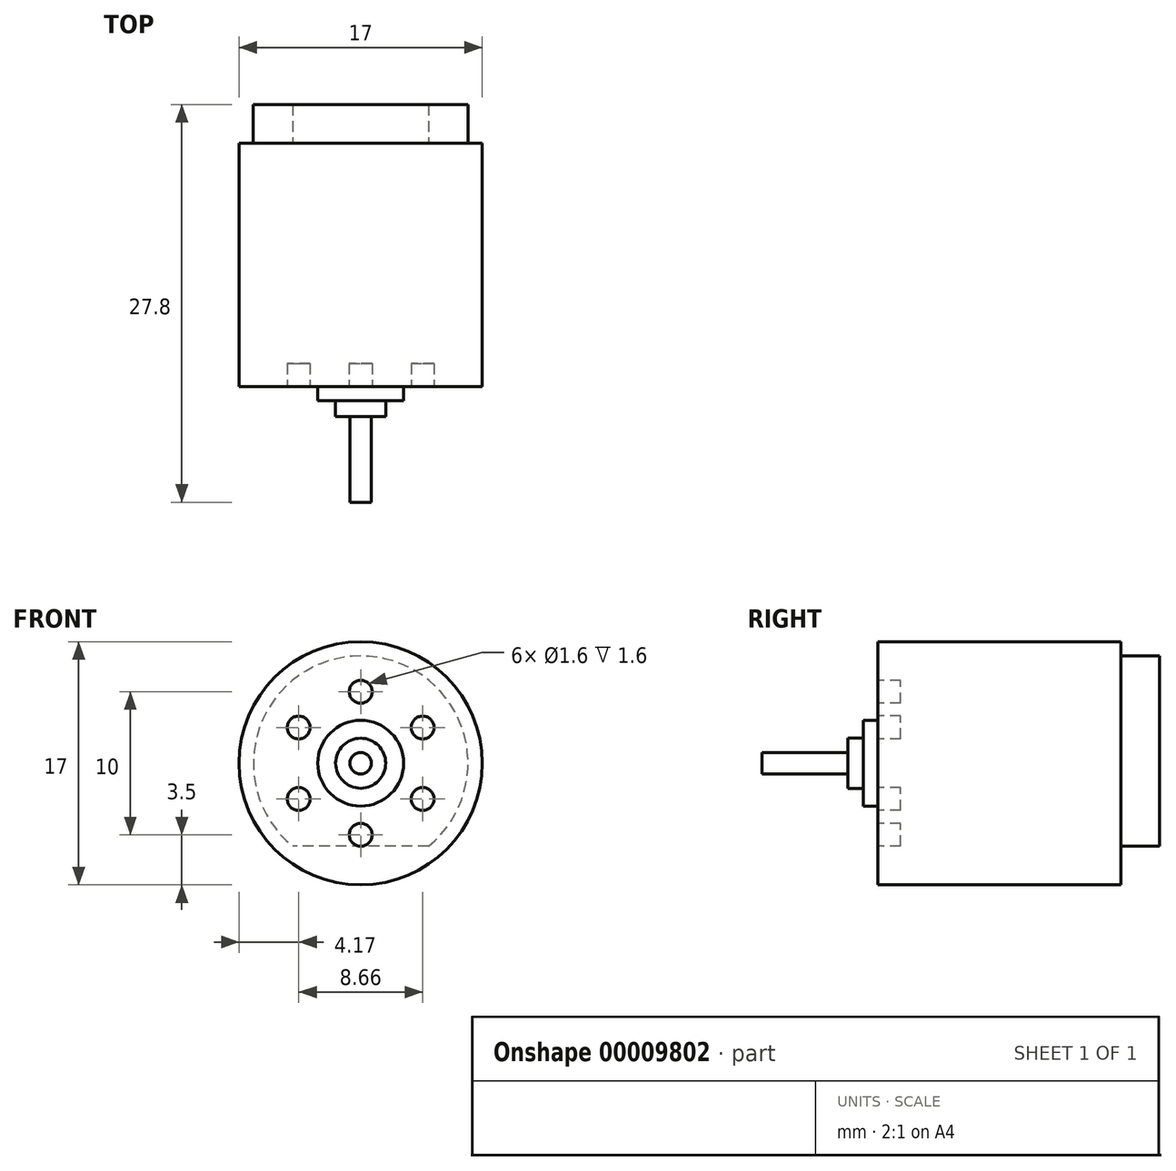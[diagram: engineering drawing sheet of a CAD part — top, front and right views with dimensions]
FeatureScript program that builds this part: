
annotation { "Feature Type Name" : "Feature", "Feature Type Description" : "" }
export const myFeature = defineFeature(function(context is Context, id is Id, definition is map)
    precondition{}
    {
        {
            var Q0;
            Q0=qCreatedBy(makeId("Front.planeOp"),FACE);
            var sketch = newSketch(context, id + "F0", { "sketchPlane" : qUnion([Q0])});
            skCircle(sketch, "E0", {"center": v(0, 0) * mm, "radius": 8.5 * mm});
            skSolve(sketch);
        }
        {
            var Q0;
            Q0=makeQuery(id+"F0.imprint","IMPRINT",FACE,{"disambiguationData":[TD([[makeQuery(id+"F0.imprint","IMPRINT",EDGE,{"derivedFrom":sQuery(id+"F0.wireOp",EDGE,"E0")}),1.0]])]});
            extrude(context, id + "F1", {"entities" : qUnion([Q0]), "depth" : 17 * mm});
        }
        {
            var Q0;
            Q0=makeQuery(id+"F1.opExtrude","CAP_FACE",FACE,{"disambiguationData":[OSD([sQuery(id+"F0.wireOp",EDGE,"E0")])],"isStart":false});
            var sketch = newSketch(context, id + "F2", { "sketchPlane" : qUnion([Q0])});
            skCircle(sketch, "E1", {"center": v(0, 5) * mm, "radius": 0.8 * mm});
            skCircle(sketch, "E2.1.0", {"center": v(-4.33, 2.5) * mm, "radius": 0.8 * mm});
            skCircle(sketch, "E2.2.0", {"center": v(-4.33, -2.5) * mm, "radius": 0.8 * mm});
            skCircle(sketch, "E2.3.0", {"center": v(0, -5) * mm, "radius": 0.8 * mm});
            skCircle(sketch, "E2.4.0", {"center": v(4.33, -2.5) * mm, "radius": 0.8 * mm});
            skCircle(sketch, "E2.5.0", {"center": v(4.33, 2.5) * mm, "radius": 0.8 * mm});
            skPoint(sketch, "E2.center", {"position": v(0, 0) * mm});
            skSolve(sketch);
        }
        {
            var Q0;
            Q0=makeQuery(id+"F2.imprint","IMPRINT",FACE,{"disambiguationData":[TD([[makeQuery(id+"F2.imprint","IMPRINT",EDGE,{"derivedFrom":sQuery(id+"F2.wireOp",EDGE,"E1")}),1.0]])]});
            var Q1;
            Q1=makeQuery(id+"F2.imprint","IMPRINT",FACE,{"disambiguationData":[TD([[makeQuery(id+"F2.imprint","IMPRINT",EDGE,{"derivedFrom":sQuery(id+"F2.wireOp",EDGE,"E2.1.0")}),1.0]])]});
            var Q2;
            Q2=makeQuery(id+"F2.imprint","IMPRINT",FACE,{"disambiguationData":[TD([[makeQuery(id+"F2.imprint","IMPRINT",EDGE,{"derivedFrom":sQuery(id+"F2.wireOp",EDGE,"E2.2.0")}),1.0]])]});
            var Q3;
            Q3=makeQuery(id+"F2.imprint","IMPRINT",FACE,{"disambiguationData":[TD([[makeQuery(id+"F2.imprint","IMPRINT",EDGE,{"derivedFrom":sQuery(id+"F2.wireOp",EDGE,"E2.3.0")}),1.0]])]});
            var Q4;
            Q4=makeQuery(id+"F2.imprint","IMPRINT",FACE,{"disambiguationData":[TD([[makeQuery(id+"F2.imprint","IMPRINT",EDGE,{"derivedFrom":sQuery(id+"F2.wireOp",EDGE,"E2.4.0")}),1.0]])]});
            var Q5;
            Q5=makeQuery(id+"F2.imprint","IMPRINT",FACE,{"disambiguationData":[TD([[makeQuery(id+"F2.imprint","IMPRINT",EDGE,{"derivedFrom":sQuery(id+"F2.wireOp",EDGE,"E2.5.0")}),1.0]])]});
            extrude(context, id + "F3", {"entities" : qUnion([Q0, Q1, Q2, Q3, Q4, Q5]), "operationType" : NewBodyOperationType.REMOVE, "oppositeDirection" : true, "depth" : 1.6 * mm});
        }
        {
            var Q0;
            Q0=makeQuery(id+"F1.opExtrude","CAP_FACE",FACE,{"disambiguationData":[OSD([sQuery(id+"F0.wireOp",EDGE,"E0")])],"isStart":false});
            var sketch = newSketch(context, id + "F4", { "sketchPlane" : qUnion([Q0])});
            skCircle(sketch, "E3", {"center": v(0, 0) * mm, "radius": 3 * mm});
            skSolve(sketch);
        }
        {
            var Q0;
            Q0=makeQuery(id+"F4.imprint","IMPRINT",FACE,{"disambiguationData":[TD([[makeQuery(id+"F4.imprint","IMPRINT",EDGE,{"derivedFrom":sQuery(id+"F4.wireOp",EDGE,"E3")}),1.0]])]});
            extrude(context, id + "F5", {"entities" : qUnion([Q0]), "operationType" : NewBodyOperationType.ADD, "depth" : 1 * mm});
        }
        {
            var Q0;
            Q0=makeQuery(id+"F5.opExtrude","CAP_FACE",FACE,{"disambiguationData":[OSD([sQuery(id+"F4.wireOp",EDGE,"E3")])],"isStart":false});
            var sketch = newSketch(context, id + "F6", { "sketchPlane" : qUnion([Q0])});
            skCircle(sketch, "E4", {"center": v(0, 0) * mm, "radius": 1.75 * mm});
            skSolve(sketch);
        }
        {
            var Q0;
            Q0=makeQuery(id+"F6.imprint","IMPRINT",FACE,{"disambiguationData":[TD([[makeQuery(id+"F6.imprint","IMPRINT",EDGE,{"derivedFrom":sQuery(id+"F6.wireOp",EDGE,"E4")}),1.0]])]});
            extrude(context, id + "F7", {"entities" : qUnion([Q0]), "operationType" : NewBodyOperationType.ADD, "depth" : 1.1 * mm});
        }
        {
            var Q0;
            Q0=makeQuery(id+"F7.opExtrude","CAP_FACE",FACE,{"disambiguationData":[OSD([sQuery(id+"F6.wireOp",EDGE,"E4")])],"isStart":false});
            var sketch = newSketch(context, id + "F8", { "sketchPlane" : qUnion([Q0])});
            skCircle(sketch, "E5", {"center": v(0, 0) * mm, "radius": 0.75 * mm});
            skSolve(sketch);
        }
        {
            var Q0;
            Q0=makeQuery(id+"F8.imprint","IMPRINT",FACE,{"disambiguationData":[TD([[makeQuery(id+"F8.imprint","IMPRINT",EDGE,{"derivedFrom":sQuery(id+"F8.wireOp",EDGE,"E5")}),1.0]])]});
            extrude(context, id + "F9", {"entities" : qUnion([Q0]), "operationType" : NewBodyOperationType.ADD, "depth" : 6 * mm});
        }
        {
            var Q0;
            Q0=makeQuery(id+"F1.opExtrude","CAP_FACE",FACE,{"disambiguationData":[OSD([sQuery(id+"F0.wireOp",EDGE,"E0")])],"isStart":true});
            var sketch = newSketch(context, id + "F10", { "sketchPlane" : qUnion([Q0])});
            skCircle(sketch, "E6", {"center": v(0, 0) * mm, "radius": 7.5 * mm});
            skLineSegment(sketch, "E7", {"start": v(-4.75, -5.8) * mm, "end": v(4.75, -5.8) * mm});
            skSolve(sketch);
        }
        {
            var Q0;
            {var subQ0=sQuery(id+"F10.wireOp",EDGE,"E7");Q0=makeQuery(id+"F10.imprint","IMPRINT",FACE,{"disambiguationData":[TD([[makeQuery(id+"F10.imprint","IMPRINT",EDGE,{"derivedFrom":subQ0}),1.0]])]});}
            extrude(context, id + "F11", {"entities" : qUnion([Q0]), "operationType" : NewBodyOperationType.ADD, "depth" : 2.7 * mm});
        }
    });
